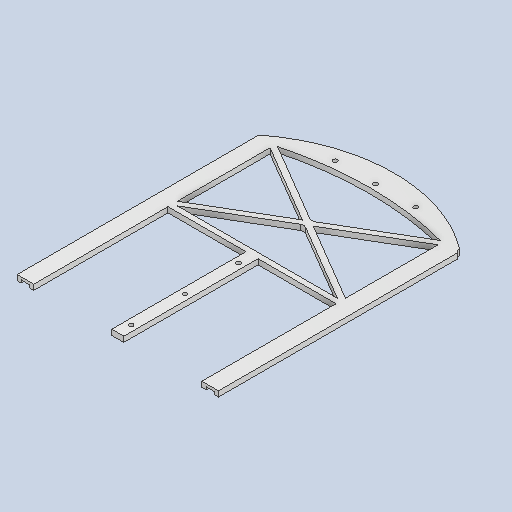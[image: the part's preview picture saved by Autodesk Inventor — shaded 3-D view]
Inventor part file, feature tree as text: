
AUTODESK INVENTOR PART (.ipt)
format: ipt  version: 2023 (Build 270158000, 158)  size: 356,352 bytes
history: native  units: mm
features: sketch x8, extrude x6, hole x2, other x1, fillet x1
ambient origin geometry x8: Origin, YZ Plane, XZ Plane, XY Plane, X Axis, Y Axis, Z Axis, Center Point
bodies: Body1 (feature_tree)
feature tree (18):
  other  "ソリッド1"
  extrude  "押し出し1"  Depth=150.0mm
  extrude  "押し出し2"  Depth=180.0mm
  extrude  "押し出し3"  Depth=4.0mm TaperAngle=0.0deg
  extrude  "押し出し4"  Depth=125.2mm
  extrude  "押し出し5"  Depth=100.0mm
  hole  "穴1"  [1 undecoded]
  extrude  "押し出し6"  Depth=4.0mm TaperAngle=0.0deg
  hole  "穴2"  [1 undecoded]
  fillet  "フィレット1"  Radius=180.0mm
  sketch  "スケッチ1"
  sketch  "スケッチ2"
  sketch  "スケッチ3"
  sketch  "スケッチ4"
  sketch  "スケッチ5"
  sketch  "スケッチ6"
  sketch  "スケッチ7"
  sketch  "スケッチ8"
note: 2 required parameter values undecoded (feature->parameter linkage not recoverable at this tier; creation-order binding heuristic only, values carry confidence <= 0.55)
